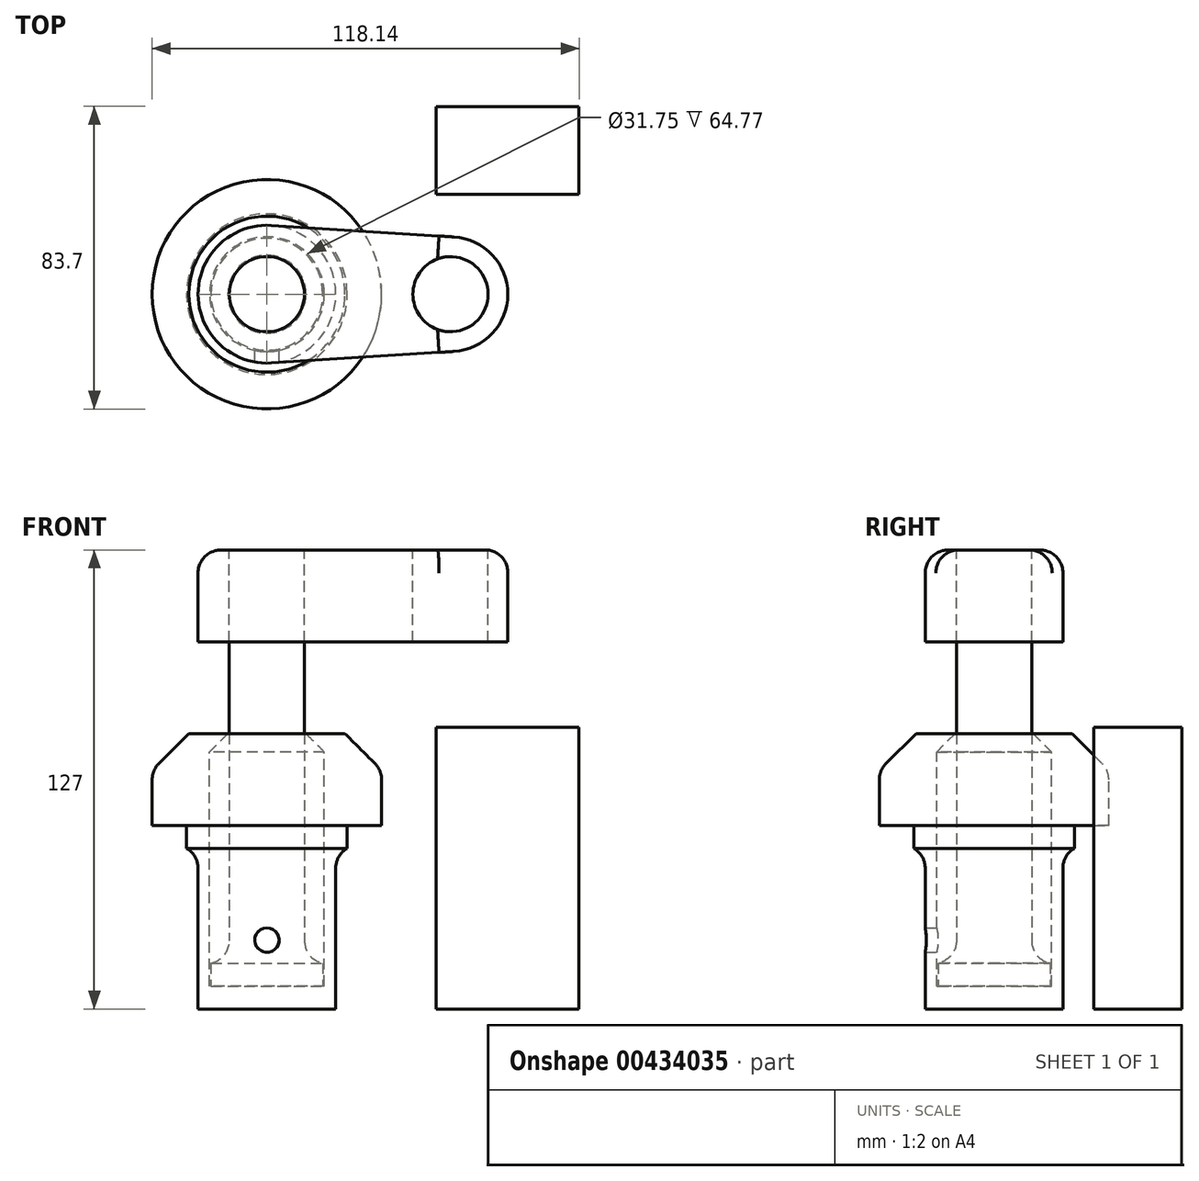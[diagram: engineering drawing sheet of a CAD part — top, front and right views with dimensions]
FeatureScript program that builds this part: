
annotation { "Feature Type Name" : "Feature", "Feature Type Description" : "" }
export const myFeature = defineFeature(function(context is Context, id is Id, definition is map)
    precondition{}
    {
        {
            var Q0;
            Q0=qCreatedBy(makeId("Front.planeOp"),FACE);
            var sketch = newSketch(context, id + "F0", { "sketchPlane" : qUnion([Q0])});
            skLineSegment(sketch, "E0", {"start": v(0, 0) * mm, "end": v(0, 76.2) * mm});
            skLineSegment(sketch, "E1", {"start": v(0, 76.2) * mm, "end": v(21.59, 76.2) * mm});
            skLineSegment(sketch, "E2", {"start": v(21.6, 76.2) * mm, "end": v(31.75, 66.04) * mm});
            skLineSegment(sketch, "E3", {"start": v(31.75, 66.04) * mm, "end": v(31.75, 50.8) * mm});
            skLineSegment(sketch, "E4", {"start": v(31.75, 50.8) * mm, "end": v(22.23, 50.8) * mm});
            skLineSegment(sketch, "E5", {"start": v(22.23, 50.8) * mm, "end": v(22.23, 44.45) * mm});
            skLineSegment(sketch, "E6", {"start": v(22.23, 44.45) * mm, "end": v(19.05, 44.45) * mm});
            skLineSegment(sketch, "E7", {"start": v(19.05, 44.45) * mm, "end": v(19.05, 0) * mm});
            skLineSegment(sketch, "E8", {"start": v(19.05, 0) * mm, "end": v(0, 0) * mm});
            skLineSegment(sketch, "E9", {"start": v(10.8, 76.2) * mm, "end": v(15.88, 71.12) * mm});
            skLineSegment(sketch, "E10", {"start": v(15.88, 71.12) * mm, "end": v(15.88, 6.35) * mm});
            skLineSegment(sketch, "E11", {"start": v(15.88, 6.35) * mm, "end": v(0, 6.35) * mm});
            skLineSegment(sketch, "E12", {"start": v(0, 76.2) * mm, "end": v(0, 89.89) * mm, "construction": true});
            skLineSegment(sketch, "E13", {"start": v(0, 76.2) * mm, "end": v(0, 127) * mm});
            skPoint(sketch, "E13.endSnap0", {"position": v(0, 83.04) * mm});
            skLineSegment(sketch, "E14", {"start": v(0, 127) * mm, "end": v(10.4, 127) * mm});
            skLineSegment(sketch, "E15", {"start": v(10.4, 127) * mm, "end": v(10.4, 12.7) * mm});
            skLineSegment(sketch, "E16", {"start": v(10.4, 12.7) * mm, "end": v(15.48, 12.7) * mm});
            skLineSegment(sketch, "E17", {"start": v(15.48, 12.7) * mm, "end": v(15.48, 6.35) * mm});
            skSolve(sketch);
        }
        {
            var Q0;
            {var subQ4=sQuery(id+"F0.wireOp",EDGE,"E2");Q0=makeQuery(id+"F0.imprint","IMPRINT",FACE,{"disambiguationData":[TD([[makeQuery(id+"F0.imprint","IMPRINT",EDGE,{"derivedFrom":subQ4}),-1.0]])]});}
            var Q1;
            Q1=sQuery(id+"F0.wireOp",EDGE,"E0");
            revolve(context, id + "F1", {"entities" : qUnion([Q0]), "axis" : qUnion([Q1]), "revolveType" : RevolveType.FULL, "oppositeDirection" : true});
        }
        {
            var Q0;
            {var subQ0=sQuery(id+"F0.wireOp",EDGE,"E13");Q0=makeQuery(id+"F0.imprint","IMPRINT",FACE,{"disambiguationData":[TD([[makeQuery(id+"F0.imprint","IMPRINT",EDGE,{"derivedFrom":subQ0}),-1.0]])]});}
            var Q1;
            {var subQ0=sQuery(id+"F0.wireOp",EDGE,"E16");Q1=makeQuery(id+"F0.imprint","IMPRINT",FACE,{"disambiguationData":[TD([[makeQuery(id+"F0.imprint","IMPRINT",EDGE,{"derivedFrom":subQ0}),-1.0]])]});}
            var Q2;
            Q2=sQuery(id+"F0.wireOp",EDGE,"E13");
            revolve(context, id + "F2", {"entities" : qUnion([Q0, Q1]), "axis" : qUnion([Q2]), "revolveType" : RevolveType.FULL});
        }
        {
            var Q0;
            Q0=makeQuery(id+"F2.opRevolve","SWEPT_FACE",FACE,{"disambiguationData":[OSD([sQuery(id+"F0.wireOp",EDGE,"E14")])]});
            var sketch = newSketch(context, id + "F3", { "sketchPlane" : qUnion([Q0])});
            skCircle(sketch, "E18", {"center": v(0, 0) * mm, "radius": 19.05 * mm});
            skCircle(sketch, "E19", {"center": v(50.8, 0) * mm, "radius": 15.88 * mm});
            skLineSegment(sketch, "E20", {"start": v(51.8, -15.84) * mm, "end": v(1.2, -19.01) * mm});
            skLineSegment(sketch, "E21", {"start": v(1.2, 19.01) * mm, "end": v(51.8, 15.84) * mm});
            skCircle(sketch, "E22.0", {"center": v(0, 0) * mm, "radius": 10.4 * mm});
            skCircle(sketch, "E23", {"center": v(50.8, 0) * mm, "radius": 10.4 * mm});
            skSolve(sketch);
        }
        {
            var Q0;
            Q0 = qSketchRegion(id + "F3", true);
            var Q1;
            Q1=makeQuery(id+"F1.opRevolve","SWEPT_FACE",FACE,{"disambiguationData":[OSD([sQuery(id+"F0.wireOp",EDGE,"E1")])]});
            extrude(context, id + "F4", {"entities" : qUnion([Q0]), "oppositeDirection" : true, "endBoundEntityFace" : qUnion([Q1]), "depth" : 25.4 * mm});
        }
        {
            var Q0;
            Q0=qCreatedBy(makeId("Front.planeOp"),FACE);
            var sketch = newSketch(context, id + "F5", { "sketchPlane" : qUnion([Q0])});
            skPoint(sketch, "E24", {"position": v(0, 19.05) * mm});
            skSolve(sketch);
        }
        {
            var Q0;
            Q0=sQuery(id+"F5.wireOp",VERTEX,"E24");
            var Q1;
            Q1=makeQuery(id+"F1.opRevolve","SWEPT_BODY",BODY,{"disambiguationData":[OSD([sQuery(id+"F0.wireOp",EDGE,"E0"),sQuery(id+"F0.wireOp",EDGE,"E1"),sQuery(id+"F0.wireOp",EDGE,"E2"),sQuery(id+"F0.wireOp",EDGE,"E3"),sQuery(id+"F0.wireOp",EDGE,"E4"),sQuery(id+"F0.wireOp",EDGE,"E5"),sQuery(id+"F0.wireOp",EDGE,"E6"),sQuery(id+"F0.wireOp",EDGE,"E7"),sQuery(id+"F0.wireOp",EDGE,"E8"),sQuery(id+"F0.wireOp",EDGE,"E9"),sQuery(id+"F0.wireOp",EDGE,"E10"),sQuery(id+"F0.wireOp",EDGE,"E11")])]});
            hole(context, id + "F6", {"style" : HoleStyle.SIMPLE, "endStyle" : HoleEndStyle.THROUGH, "oppositeDirection" : true, "standardTappedOrClearance" : lookupTablePath({ "standard" : "ANSI", "fit" : "Normal (ASME)", "size" : "1/4", "type" : "Clearance" }), "standardBlindInLast" : lookupTablePath({ "fit" : "Free", "standard" : "ANSI", "size" : "1/4", "type" : "Clearance" }), "holeDiameter" : 6.76 * mm, "isTappedThrough" : true, "tappedDepth" : 8.9 * mm, "tapClearance" : 3, "locations" : qUnion([Q0]), "scope" : qUnion([Q1])});
        }
        {
            var Q0;
            Q0=makeQuery(id+"F4.opExtrude","CAP_EDGE",EDGE,{"disambiguationData":[OSD([sQuery(id+"F3.wireOp",EDGE,"E21")])],"isStart":true});
            var Q1;
            Q1=makeQuery(id+"F1.opRevolve","SWEPT_EDGE",EDGE,{"disambiguationData":[OSD([sQuery(id+"F0.wireOp",EDGE,"E2"),sQuery(id+"F0.wireOp",EDGE,"E3")])]});
            var Q2;
            Q2=makeQuery(id+"F2.opRevolve","SWEPT_EDGE",EDGE,{"disambiguationData":[OSD([sQuery(id+"F0.wireOp",EDGE,"E15"),sQuery(id+"F0.wireOp",EDGE,"E16")])]});
            var Q3;
            Q3=makeQuery(id+"F1.opRevolve","SWEPT_EDGE",EDGE,{"disambiguationData":[OSD([sQuery(id+"F0.wireOp",EDGE,"E6"),sQuery(id+"F0.wireOp",EDGE,"E7")])]});
            fillet(context, id + "F7", {"entities" : qUnion([Q0, Q1, Q2, Q3]), "radius" : 6.35 * mm, "tangentPropagation" : true, "allowEdgeOverflow" : false});
        }
        {
            var Q0;
            Q0=makeQuery(id+"F1.opRevolve","SWEPT_FACE",FACE,{"disambiguationData":[OSD([sQuery(id+"F0.wireOp",EDGE,"E8")])]});
            var sketch = newSketch(context, id + "F8", { "sketchPlane" : qUnion([Q0])});
            skLineSegment(sketch, "E25.bottom", {"start": v(86.39, -27.65) * mm, "end": v(46.84, -27.65) * mm});
            skLineSegment(sketch, "E25.top", {"start": v(86.39, -51.95) * mm, "end": v(46.84, -51.95) * mm});
            skLineSegment(sketch, "E25.left", {"start": v(86.39, -27.65) * mm, "end": v(86.39, -51.95) * mm});
            skLineSegment(sketch, "E25.right", {"start": v(46.84, -27.65) * mm, "end": v(46.84, -51.95) * mm});
            skPoint(sketch, "E25.middle", {"position": v(66.61, -39.8) * mm});
            skSolve(sketch);
        }
        {
            var Q0;
            Q0 = qSketchRegion(id + "F8", true);
            extrude(context, id + "F9", {"entities" : qUnion([Q0]), "oppositeDirection" : true, "depth" : 25.4 * mm});
        }
        {
            var Q0;
            Q0=makeQuery(id+"F9.opExtrude","CAP_FACE",FACE,{"disambiguationData":[OSD([sQuery(id+"F8.wireOp",EDGE,"E25.bottom"),sQuery(id+"F8.wireOp",EDGE,"E25.top"),sQuery(id+"F8.wireOp",EDGE,"E25.left"),sQuery(id+"F8.wireOp",EDGE,"E25.right")])],"isStart":false});
            extrude(context, id + "F10", {"entities" : qUnion([Q0]), "operationType" : NewBodyOperationType.ADD, "depth" : 52.58 * mm});
        }
    });
